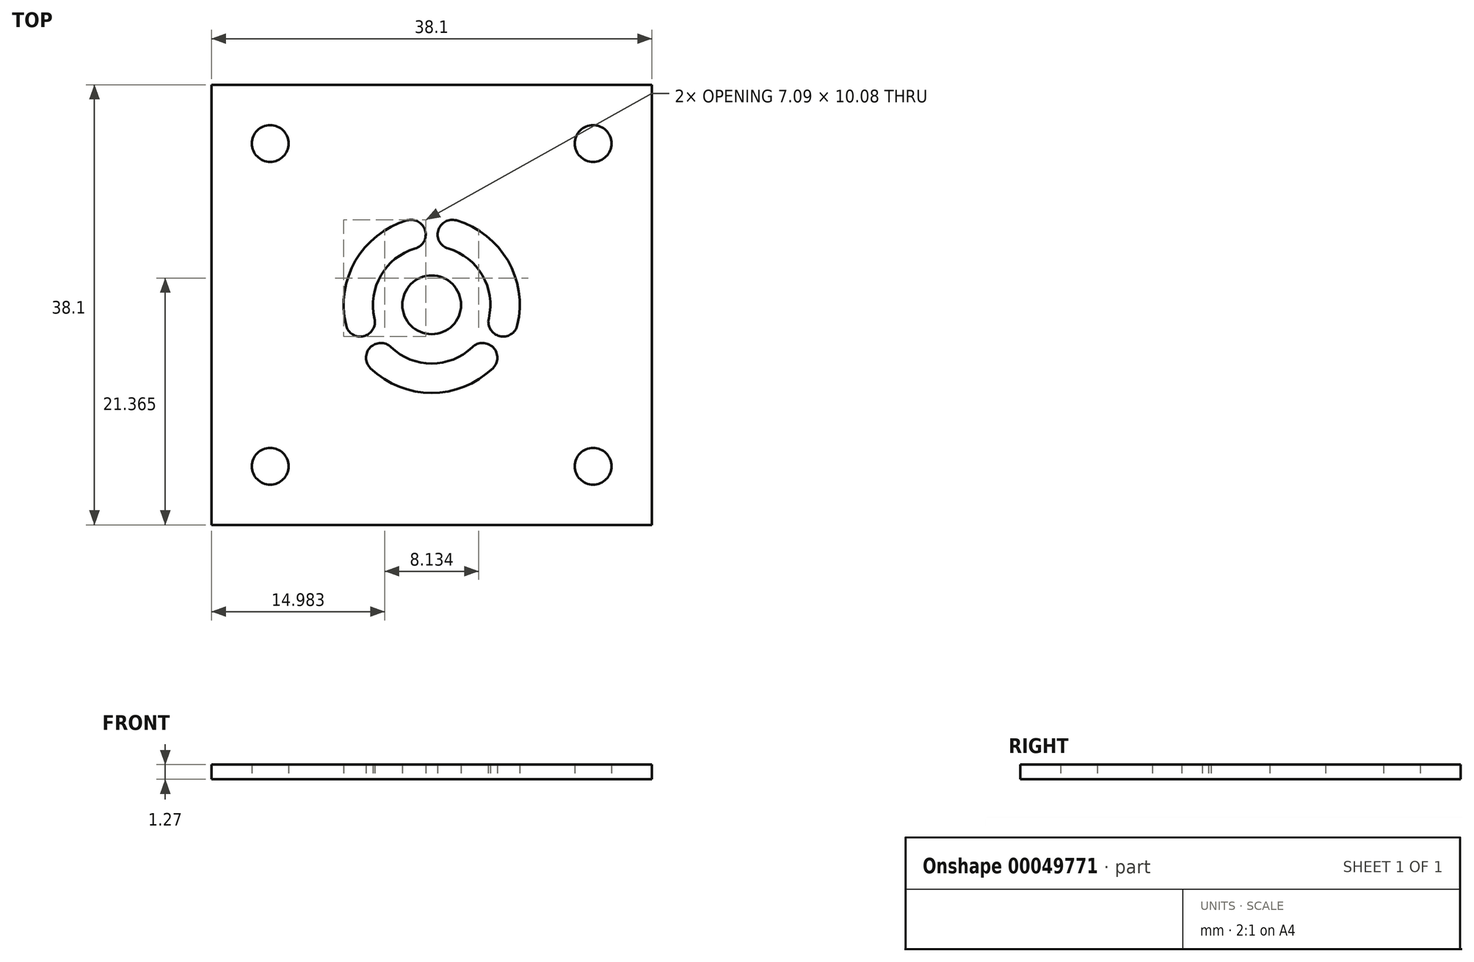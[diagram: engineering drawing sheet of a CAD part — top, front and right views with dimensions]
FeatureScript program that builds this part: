
annotation { "Feature Type Name" : "Feature", "Feature Type Description" : "" }
export const myFeature = defineFeature(function(context is Context, id is Id, definition is map)
    precondition{}
    {
        {
            var Q0;
            Q0=qCreatedBy(makeId("Top.planeOp"),FACE);
            var sketch = newSketch(context, id + "F0", { "sketchPlane" : qUnion([Q0])});
            skLineSegment(sketch, "E0.rect.bottom", {"start": v(19.05, -19.05) * mm, "end": v(-19.05, -19.05) * mm});
            skLineSegment(sketch, "E0.rect.top", {"start": v(19.05, 19.05) * mm, "end": v(-19.05, 19.05) * mm});
            skLineSegment(sketch, "E0.rect.left", {"start": v(19.05, -19.05) * mm, "end": v(19.05, 19.05) * mm});
            skLineSegment(sketch, "E0.rect.right", {"start": v(-19.05, -19.05) * mm, "end": v(-19.05, 19.05) * mm});
            skPoint(sketch, "E0.rect.middle", {"position": v(0, 0) * mm});
            skSolve(sketch);
        }
        {
            var Q0;
            Q0=qSketchRegion(id+"F0",true);
            extrude(context, id + "F1", {"entities" : qUnion([Q0]), "depth" : 1.27 * mm});
        }
        {
            var Q0;
            Q0=qCreatedBy(makeId("Top.planeOp"),FACE);
            var sketch = newSketch(context, id + "F2", { "sketchPlane" : qUnion([Q0])});
            skLineSegment(sketch, "E1", {"start": v(0.52, 6.2) * mm, "end": v(0.52, 6.2) * mm});
            skLineSegment(sketch, "E2", {"start": v(-0.52, 6.2) * mm, "end": v(-0.52, 6.2) * mm});
            skLineSegment(sketch, "E3", {"start": v(5.13, -3.52) * mm, "end": v(5.13, -3.52) * mm});
            skLineSegment(sketch, "E4", {"start": v(5.64, -2.62) * mm, "end": v(5.64, -2.62) * mm});
            skLineSegment(sketch, "E5", {"start": v(-5.64, -2.62) * mm, "end": v(-5.64, -2.62) * mm});
            skLineSegment(sketch, "E6", {"start": v(-5.13, -3.52) * mm, "end": v(-5.13, -3.52) * mm});
            skArc(sketch, "E7", {"start": v(-2.14, 7.31) * mm, "mid": v(-6.6, 3.83) * mm, "end": v(-7.41, -1.77) * mm});
            skArc(sketch, "E8", {"start": v(7.41, -1.77) * mm, "mid": v(6.6, 3.83) * mm, "end": v(2.14, 7.31) * mm});
            skArc(sketch, "E9", {"start": v(-5.29, -5.49) * mm, "mid": v(0, -7.62) * mm, "end": v(5.29, -5.49) * mm});
            skArc(sketch, "E10", {"start": v(-1.43, 4.88) * mm, "mid": v(-4.4, 2.55) * mm, "end": v(-4.94, -1.18) * mm});
            skArc(sketch, "E11", {"start": v(4.94, -1.18) * mm, "mid": v(4.4, 2.55) * mm, "end": v(1.43, 4.88) * mm});
            skArc(sketch, "E12", {"start": v(-3.53, -3.66) * mm, "mid": v(0, -5.08) * mm, "end": v(3.53, -3.66) * mm});
            skPoint(sketch, "E13.visualSharp", {"position": v(-6.9, -3.21) * mm});
            skArc(sketch, "E13.filletArc", {"start": v(-7.41, -1.77) * mm, "mid": v(-6.73, -2.62) * mm, "end": v(-5.64, -2.62) * mm});
            skPoint(sketch, "E14.visualSharp", {"position": v(-4.6, -2.14) * mm});
            skArc(sketch, "E14.filletArc", {"start": v(-5.64, -2.62) * mm, "mid": v(-5.03, -2.03) * mm, "end": v(-4.94, -1.18) * mm});
            skPoint(sketch, "E15.visualSharp", {"position": v(-0.64, 7.6) * mm});
            skArc(sketch, "E15.filletArc", {"start": v(-0.52, 6.2) * mm, "mid": v(-1.07, 7.14) * mm, "end": v(-2.14, 7.31) * mm});
            skPoint(sketch, "E16.visualSharp", {"position": v(-0.42, 5.06) * mm});
            skArc(sketch, "E16.filletArc", {"start": v(-1.43, 4.88) * mm, "mid": v(-0.74, 5.38) * mm, "end": v(-0.52, 6.2) * mm});
            skPoint(sketch, "E17.visualSharp", {"position": v(0.42, 5.06) * mm});
            skArc(sketch, "E17.filletArc", {"start": v(0.52, 6.2) * mm, "mid": v(0.74, 5.38) * mm, "end": v(1.43, 4.88) * mm});
            skPoint(sketch, "E18.visualSharp", {"position": v(0.64, 7.6) * mm});
            skArc(sketch, "E18.filletArc", {"start": v(2.14, 7.31) * mm, "mid": v(1.07, 7.14) * mm, "end": v(0.52, 6.2) * mm});
            skPoint(sketch, "E19.visualSharp", {"position": v(4.6, -2.14) * mm});
            skArc(sketch, "E19.filletArc", {"start": v(4.94, -1.18) * mm, "mid": v(5.03, -2.03) * mm, "end": v(5.64, -2.62) * mm});
            skPoint(sketch, "E20.visualSharp", {"position": v(6.9, -3.21) * mm});
            skArc(sketch, "E20.filletArc", {"start": v(5.64, -2.62) * mm, "mid": v(6.73, -2.62) * mm, "end": v(7.41, -1.77) * mm});
            skPoint(sketch, "E21.visualSharp", {"position": v(4.19, -2.88) * mm});
            skArc(sketch, "E21.filletArc", {"start": v(5.13, -3.52) * mm, "mid": v(4.3, -3.3) * mm, "end": v(3.53, -3.66) * mm});
            skPoint(sketch, "E22.visualSharp", {"position": v(6.28, -4.32) * mm});
            skArc(sketch, "E22.filletArc", {"start": v(5.29, -5.49) * mm, "mid": v(5.67, -4.47) * mm, "end": v(5.13, -3.52) * mm});
            skPoint(sketch, "E23.visualSharp", {"position": v(-6.28, -4.32) * mm});
            skArc(sketch, "E23.filletArc", {"start": v(-5.13, -3.52) * mm, "mid": v(-5.67, -4.47) * mm, "end": v(-5.29, -5.49) * mm});
            skPoint(sketch, "E24.visualSharp", {"position": v(-4.19, -2.88) * mm});
            skArc(sketch, "E24.filletArc", {"start": v(-3.53, -3.66) * mm, "mid": v(-4.3, -3.3) * mm, "end": v(-5.13, -3.52) * mm});
            skSolve(sketch);
        }
        {
            var Q0;
            Q0=qSketchRegion(id+"F2",true);
            extrude(context, id + "F3", {"entities" : qUnion([Q0]), "operationType" : NewBodyOperationType.REMOVE, "depth" : 25.4 * mm});
        }
        {
            var Q0;
            Q0=qCreatedBy(makeId("Top.planeOp"),FACE);
            var sketch = newSketch(context, id + "F4", { "sketchPlane" : qUnion([Q0])});
            skCircle(sketch, "E25", {"center": v(13.97, 13.97) * mm, "radius": 1.59 * mm});
            skCircle(sketch, "E26", {"center": v(13.97, -13.97) * mm, "radius": 1.59 * mm});
            skCircle(sketch, "E27", {"center": v(-13.97, -13.97) * mm, "radius": 1.59 * mm});
            skCircle(sketch, "E28", {"center": v(-13.97, 13.97) * mm, "radius": 1.59 * mm});
            skCircle(sketch, "E29", {"center": v(0, 0) * mm, "radius": 2.54 * mm});
            skSolve(sketch);
        }
        {
            var Q0;
            Q0=qSketchRegion(id+"F4",true);
            extrude(context, id + "F5", {"entities" : qUnion([Q0]), "operationType" : NewBodyOperationType.REMOVE, "depth" : 25.4 * mm});
        }
    });
